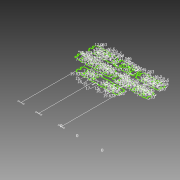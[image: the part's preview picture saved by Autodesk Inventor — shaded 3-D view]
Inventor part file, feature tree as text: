
AUTODESK INVENTOR PART (.ipt)
format: ipt  version: 2012 (Build 160160000, 160)  size: 280,576 bytes
history: native  units: mm
features: sketch x1
ambient origin geometry x8: Origin, YZ Plane, XZ Plane, XY Plane, X Axis, Y Axis, Z Axis, Center Point
feature tree (1):
  sketch  "Sketch1"  dims[d289=15.52235mm d290=2.0mm d291=15.0mm d292=15.0mm d293=15.0mm d294=15.0mm d295=15.0mm d296=15.0mm d297=15.0mm d298=7.0mm d299=30.0mm d300=121.522mm d307=7.675mm d308=7.675mm d309=11.7mm d310=6.9mm d311=23.4mm d312=11.7mm d313=6.9mm d314=7.675mm d315=7.675mm d316=7.8mm d317=7.8mm d318=38.75mm d320=7.675mm d321=7.675mm d322=11.7mm d323=6.9mm d324=23.4mm d325=11.7mm d326=6.9mm d327=7.675mm d328=7.675mm d329=7.8mm d330=7.8mm d331=38.75mm d371=33.0mm d372=33.0mm d373=0.0mm d413=12.063446mm d415=2.0mm d416=10.0mm d417=10.0mm d418=10.0mm d419=10.0mm d420=10.0mm d421=21.354415mm d422=30.0mm d423=6.0mm d424=6.0mm d425=6.0mm d429=16.5mm d430=16.5mm d431=5.9mm d432=3.0mm d433=7.8mm d434=7.8mm d435=23.4mm d436=7.675mm d437=7.675mm d438=7.675mm d439=7.675mm d440=7.8mm d441=7.8mm d442=11.7mm d443=6.9mm d444=11.7mm d445=12.063446mm d446=2.0mm d447=10.0mm d448=10.0mm d449=10.0mm d450=10.0mm d451=10.0mm d452=21.354415mm d453=30.0mm d454=6.0mm d455=6.0mm d456=6.0mm d457=16.5mm d458=16.5mm d459=5.9mm d460=3.0mm d461=7.8mm d462=7.8mm d463=23.4mm d464=7.675mm d465=7.675mm d466=7.675mm d467=7.675mm d468=7.8mm d469=7.8mm d470=11.7mm d471=6.9mm d472=11.7mm d473=11.545619mm d476=10.0mm d478=10.0mm d481=11.545619mm d482=2.0mm d483=10.0mm d484=2.0mm d485=10.0mm d486=2.0mm d487=2.0mm d488=2.0mm d489=10.0mm d490=2.0mm d491=6.0mm d492=67.091238mm d495=15.52235mm d496=2.0mm d497=15.0mm d498=15.0mm d499=15.0mm d500=15.0mm d501=15.0mm d502=15.0mm d503=15.0mm d504=7.0mm d505=30.0mm d506=121.522mm d507=7.675mm d508=7.675mm d509=11.7mm d510=6.9mm d511=23.4mm d512=11.7mm d513=6.9mm d514=7.675mm d515=7.675mm d516=7.8mm d517=7.8mm d518=38.75mm d519=7.675mm d520=7.675mm d521=11.7mm d522=6.9mm d523=23.4mm d524=11.7mm d525=6.9mm d526=7.675mm d527=7.675mm d528=7.8mm d529=7.8mm d530=38.75mm d531=33.0mm d532=33.0mm d533=0.0mm d534=2.0mm d535=16.5mm d536=16.5mm d537=5.9mm d538=3.0mm d539=7.8mm d540=7.8mm d541=7.675mm d542=7.675mm d543=7.675mm d544=7.8mm d545=7.8mm d546=11.7mm d547=6.9mm d548=11.7mm d549=7.675mm d550=7.675mm d551=11.7mm d552=6.9mm d553=23.4mm d554=11.7mm d555=6.9mm d556=7.675mm d557=7.675mm d558=15.0mm d559=15.0mm d560=15.0mm d561=15.0mm d562=18.0mm d563=18.0mm d564=30.0mm d565=6.0mm d566=6.0mm d567=17.0mm d568=19.836667mm d569=0.0mm d570=19.673333mm d571=0.0mm d572=0.0mm]
